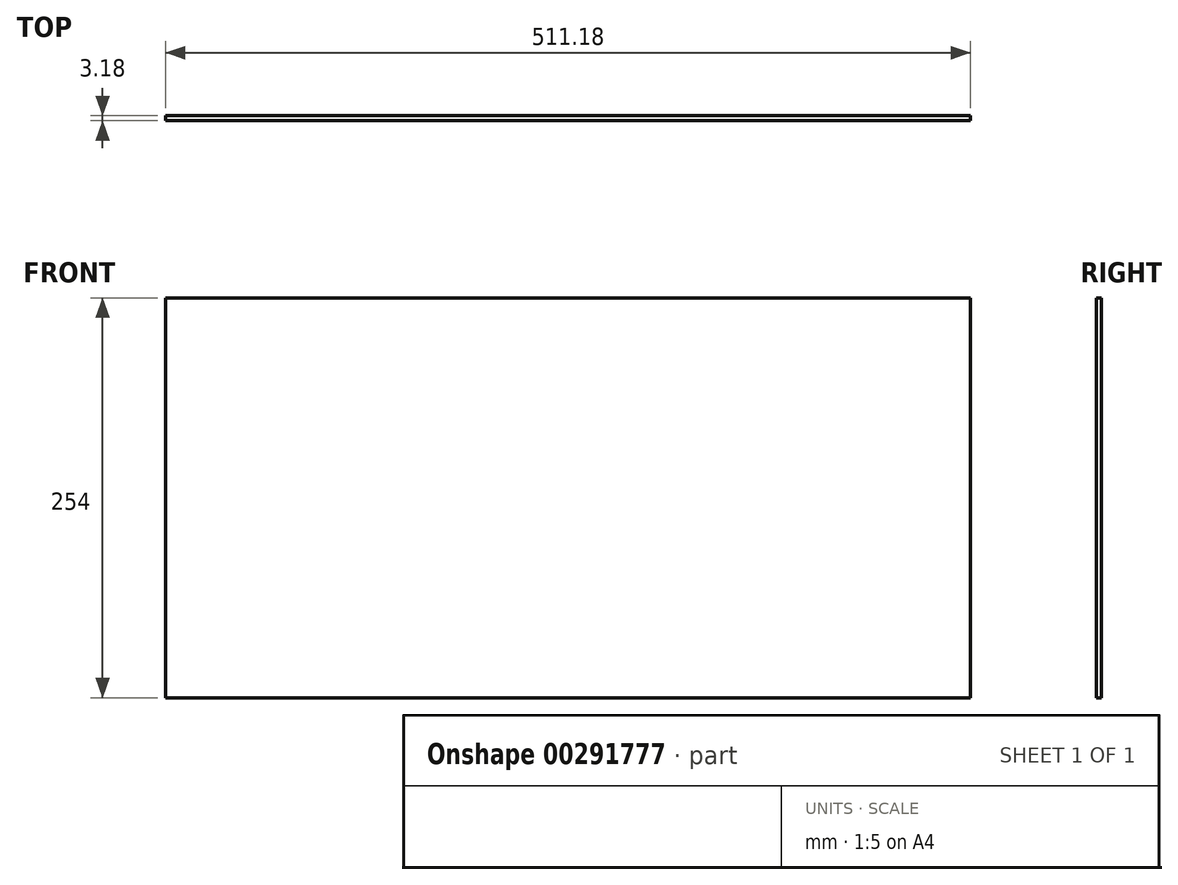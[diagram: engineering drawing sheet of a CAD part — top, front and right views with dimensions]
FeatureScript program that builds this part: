
annotation { "Feature Type Name" : "Feature", "Feature Type Description" : "" }
export const myFeature = defineFeature(function(context is Context, id is Id, definition is map)
    precondition{}
    {
        {
            var Q0;
            Q0=qCreatedBy(makeId("Front.planeOp"),FACE);
            var sketch = newSketch(context, id + "F0", { "sketchPlane" : qUnion([Q0])});
            skLineSegment(sketch, "E0.bottom", {"start": v(-253.84, -140.61) * mm, "end": v(257.34, -140.61) * mm});
            skLineSegment(sketch, "E0.top", {"start": v(-253.84, -394.61) * mm, "end": v(257.34, -394.61) * mm});
            skLineSegment(sketch, "E0.left", {"start": v(-253.84, -140.61) * mm, "end": v(-253.84, -394.61) * mm});
            skLineSegment(sketch, "E0.right", {"start": v(257.34, -140.61) * mm, "end": v(257.34, -394.61) * mm});
            skSolve(sketch);
        }
        {
            var Q0;
            Q0 = qSketchRegion(id + "F0", true);
            extrude(context, id + "F1", {"entities" : qUnion([Q0]), "endBound" : BoundingType.SYMMETRIC, "depth" : 3.17 * mm});
        }
    });
